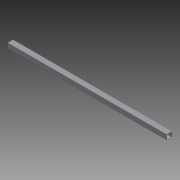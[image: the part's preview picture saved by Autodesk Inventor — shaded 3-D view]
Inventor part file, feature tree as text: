
AUTODESK INVENTOR PART (.ipt)
format: ipt  version: 2015 SP1 (Build 190203100, 203)  size: 84,480 bytes
history: native  units: in
note: dims shown in document units (in); Inventor stores cm internally (conversion verified against a paired STEP export)
features: extrude x1, fillet x1, sketch x1
ambient origin geometry x8: Origin, YZ Plane, XZ Plane, XY Plane, X Axis, Y Axis, Z Axis, Center Point
bodies: Solid1 (feature_tree)
feature tree (3):
  extrude  "Extrusion1"  Depth=2.0in
  fillet  "Fillet1"  Radius=0.083in
  sketch  "Sketch1"  dims[d0=2.0in d1=2.0in d2=0.083in d3=60.0in d4=0.0in d5=0.125in]
